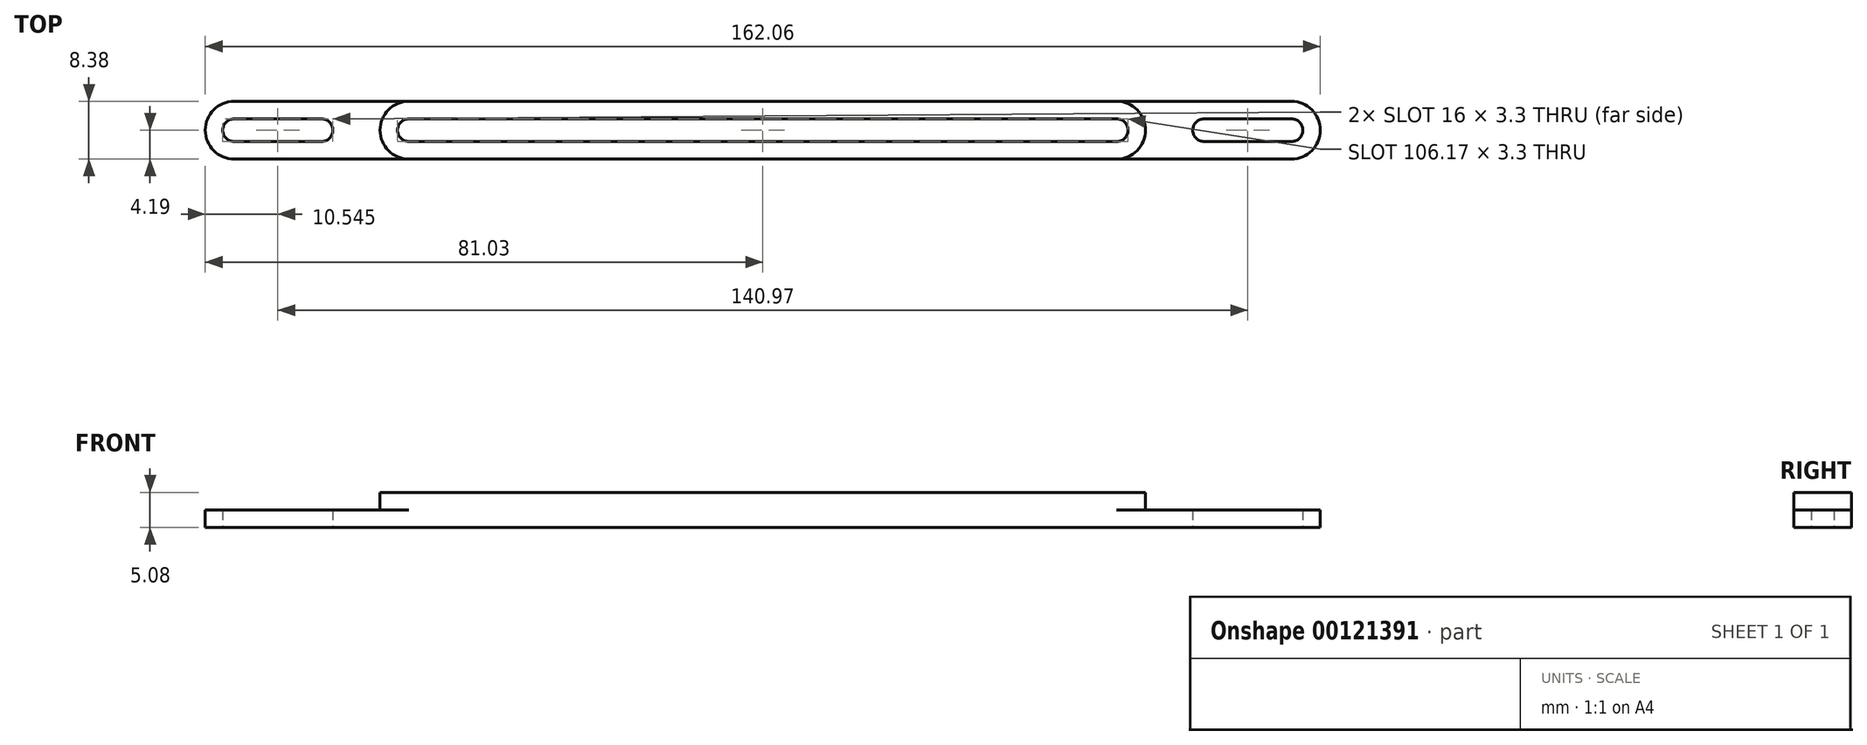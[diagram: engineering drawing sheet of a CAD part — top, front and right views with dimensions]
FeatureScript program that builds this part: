
annotation { "Feature Type Name" : "Feature", "Feature Type Description" : "" }
export const myFeature = defineFeature(function(context is Context, id is Id, definition is map)
    precondition{}
    {
        {
            var Q0;
            Q0=qCreatedBy(makeId("Top.planeOp"),FACE);
            var sketch = newSketch(context, id + "F0", { "sketchPlane" : qUnion([Q0])});
            skCircle(sketch, "E0", {"center": v(-76.83, 0) * mm, "radius": 1.65 * mm, "construction": true});
            skCircle(sketch, "E1", {"center": v(76.83, 0) * mm, "radius": 1.65 * mm, "construction": true});
            skLineSegment(sketch, "E2", {"start": v(76.84, 0) * mm, "end": v(-76.83, 0) * mm, "construction": true});
            skPoint(sketch, "E3", {"position": v(0, 0) * mm});
            skLineSegment(sketch, "E4", {"start": v(-76.83, 1.65) * mm, "end": v(-64.13, 1.65) * mm});
            skLineSegment(sketch, "E5", {"start": v(-76.83, -1.65) * mm, "end": v(-64.13, -1.65) * mm});
            skLineSegment(sketch, "E6", {"start": v(-76.83, 0) * mm, "end": v(-76.83, 1.65) * mm, "construction": true});
            skLineSegment(sketch, "E7", {"start": v(-76.83, 0) * mm, "end": v(-76.83, -1.65) * mm, "construction": true});
            skArc(sketch, "E8", {"start": v(-76.83, 1.65) * mm, "mid": v(-78.49, 0) * mm, "end": v(-76.83, -1.65) * mm});
            skArc(sketch, "E9", {"start": v(76.83, -1.65) * mm, "mid": v(78.49, 0) * mm, "end": v(76.83, 1.65) * mm});
            skLineSegment(sketch, "E10", {"start": v(-76.83, 4.2) * mm, "end": v(76.83, 4.2) * mm});
            skLineSegment(sketch, "E11", {"start": v(76.83, -4.2) * mm, "end": v(-76.83, -4.2) * mm});
            skLineSegment(sketch, "E12", {"start": v(-76.83, 1.65) * mm, "end": v(-76.83, 4.2) * mm, "construction": true});
            skLineSegment(sketch, "E13", {"start": v(-76.83, -1.65) * mm, "end": v(-76.83, -4.2) * mm, "construction": true});
            skArc(sketch, "E14", {"start": v(-76.83, 4.2) * mm, "mid": v(-81.03, 0) * mm, "end": v(-76.83, -4.2) * mm});
            skArc(sketch, "E15", {"start": v(76.83, -4.2) * mm, "mid": v(81.03, 0) * mm, "end": v(76.83, 4.2) * mm});
            skLineSegment(sketch, "E16", {"start": v(-64.13, 1.65) * mm, "end": v(-51.44, 1.65) * mm, "construction": true});
            skLineSegment(sketch, "E17", {"start": v(-64.13, -1.65) * mm, "end": v(-51.44, -1.65) * mm, "construction": true});
            skLineSegment(sketch, "E18", {"start": v(-51.44, -1.65) * mm, "end": v(51.44, -1.65) * mm});
            skLineSegment(sketch, "E19", {"start": v(-51.44, 1.65) * mm, "end": v(51.44, 1.65) * mm});
            skLineSegment(sketch, "E20", {"start": v(64.13, 1.65) * mm, "end": v(76.83, 1.65) * mm});
            skLineSegment(sketch, "E21", {"start": v(64.13, -1.65) * mm, "end": v(76.83, -1.65) * mm});
            skLineSegment(sketch, "E22", {"start": v(51.44, -1.65) * mm, "end": v(64.13, -1.65) * mm, "construction": true});
            skLineSegment(sketch, "E23", {"start": v(51.44, 1.65) * mm, "end": v(64.13, 1.65) * mm, "construction": true});
            skArc(sketch, "E24", {"start": v(-64.13, -1.65) * mm, "mid": v(-62.48, 0) * mm, "end": v(-64.13, 1.65) * mm});
            skArc(sketch, "E25", {"start": v(-51.44, 1.65) * mm, "mid": v(-53.09, 0) * mm, "end": v(-51.44, -1.65) * mm});
            skArc(sketch, "E26", {"start": v(51.44, -1.65) * mm, "mid": v(53.09, 0) * mm, "end": v(51.44, 1.65) * mm});
            skArc(sketch, "E27", {"start": v(64.13, 1.65) * mm, "mid": v(62.48, 0) * mm, "end": v(64.13, -1.65) * mm});
            skSolve(sketch);
        }
        {
            var Q0;
            Q0 = qSketchRegion(id + "F0", true);
            extrude(context, id + "F1", {"entities" : qUnion([Q0]), "depth" : 2.54 * mm});
        }
        {
            var Q0;
            Q0=makeQuery(id+"F1.opExtrude","CAP_FACE",FACE,{"disambiguationData":[OSD([sQuery(id+"F0.wireOp",EDGE,"E4"),sQuery(id+"F0.wireOp",EDGE,"E5"),sQuery(id+"F0.wireOp",EDGE,"E8"),sQuery(id+"F0.wireOp",EDGE,"E9"),sQuery(id+"F0.wireOp",EDGE,"E10"),sQuery(id+"F0.wireOp",EDGE,"E11"),sQuery(id+"F0.wireOp",EDGE,"E14"),sQuery(id+"F0.wireOp",EDGE,"E15"),sQuery(id+"F0.wireOp",EDGE,"E18"),sQuery(id+"F0.wireOp",EDGE,"E19"),sQuery(id+"F0.wireOp",EDGE,"E20"),sQuery(id+"F0.wireOp",EDGE,"E21"),sQuery(id+"F0.wireOp",EDGE,"E24"),sQuery(id+"F0.wireOp",EDGE,"E25"),sQuery(id+"F0.wireOp",EDGE,"E26"),sQuery(id+"F0.wireOp",EDGE,"E27")])],"isStart":false});
            var sketch = newSketch(context, id + "F2", { "sketchPlane" : qUnion([Q0])});
            skLineSegment(sketch, "E28", {"start": v(-51.43, 4.2) * mm, "end": v(51.44, 4.2) * mm});
            skLineSegment(sketch, "E29", {"start": v(-51.44, -4.2) * mm, "end": v(51.44, -4.2) * mm});
            skArc(sketch, "E30", {"start": v(-51.43, 4.2) * mm, "mid": v(-55.63, 0) * mm, "end": v(-51.44, -4.2) * mm});
            skArc(sketch, "E31", {"start": v(51.44, -4.2) * mm, "mid": v(55.63, 0) * mm, "end": v(51.44, 4.2) * mm});
            skLineSegment(sketch, "E32", {"start": v(-51.43, 1.65) * mm, "end": v(51.44, 1.65) * mm});
            skLineSegment(sketch, "E33", {"start": v(51.44, -1.65) * mm, "end": v(-51.43, -1.65) * mm});
            skArc(sketch, "E34", {"start": v(-51.44, 1.65) * mm, "mid": v(-53.09, 0) * mm, "end": v(-51.44, -1.65) * mm});
            skArc(sketch, "E35", {"start": v(51.44, -1.65) * mm, "mid": v(53.09, 0) * mm, "end": v(51.44, 1.65) * mm});
            skSolve(sketch);
        }
        {
            var Q0;
            Q0 = qSketchRegion(id + "F2", true);
            extrude(context, id + "F3", {"entities" : qUnion([Q0]), "operationType" : NewBodyOperationType.ADD, "depth" : 2.54 * mm});
        }
    });
